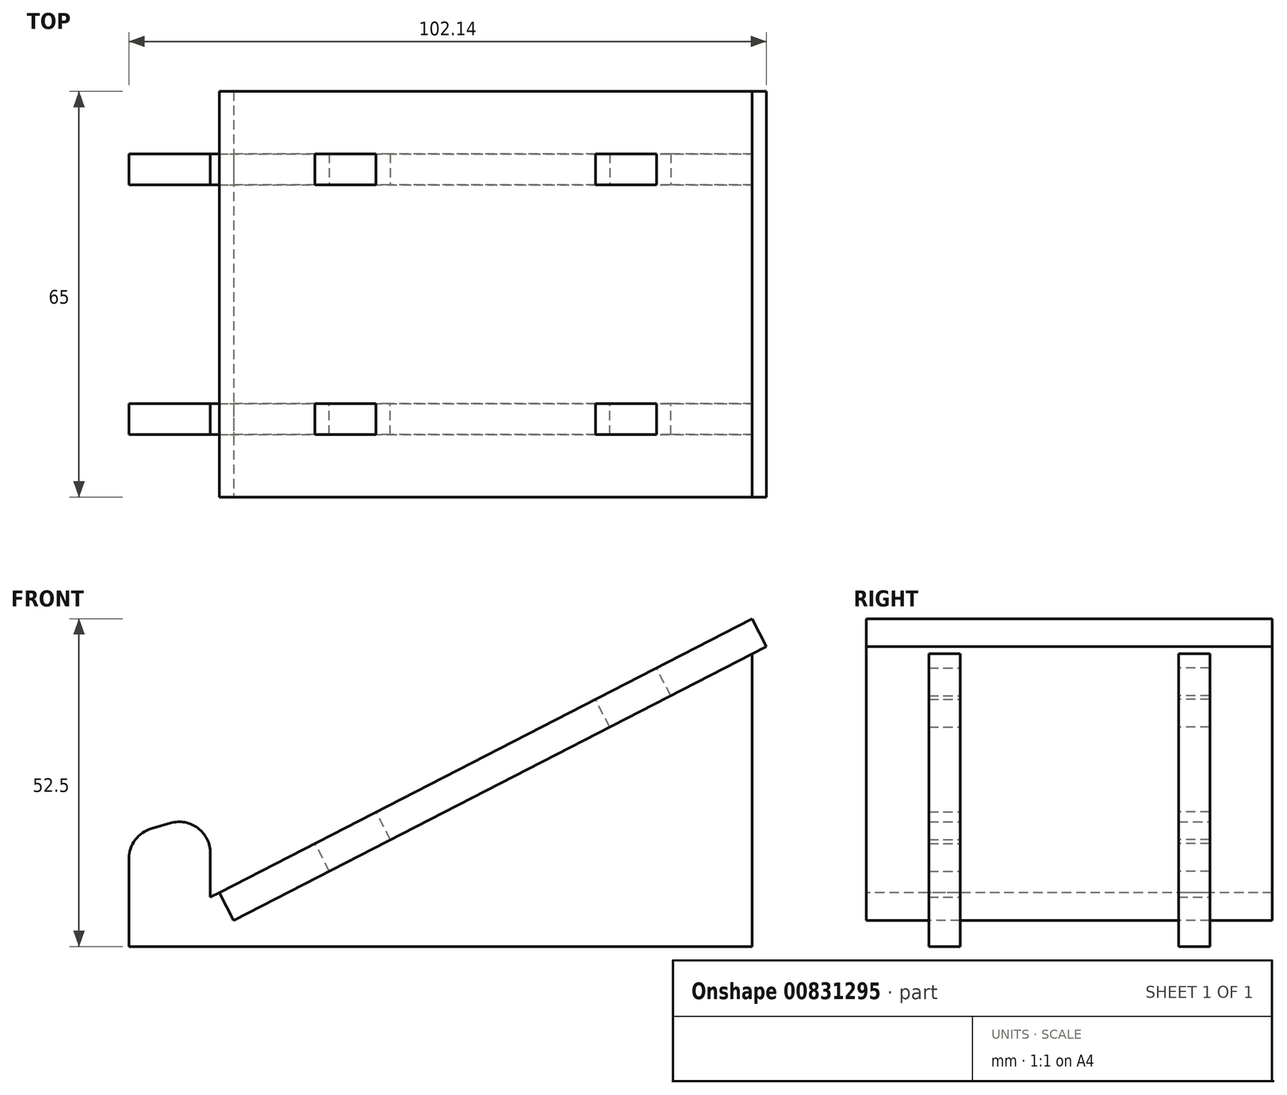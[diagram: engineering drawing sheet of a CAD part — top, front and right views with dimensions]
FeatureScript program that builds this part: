
annotation { "Feature Type Name" : "Feature", "Feature Type Description" : "" }
export const myFeature = defineFeature(function(context is Context, id is Id, definition is map)
    precondition{}
    {
        {
            var Q0;
            Q0=qCreatedBy(makeId("Front.planeOp"),FACE);
            var sketch = newSketch(context, id + "F0", { "sketchPlane" : qUnion([Q0])});
            skLineSegment(sketch, "E0", {"start": v(41.7, 0) * mm, "end": v(41.7, 52.5) * mm});
            skLineSegment(sketch, "E1", {"start": v(41.7, 52.5) * mm, "end": v(-45.12, 7.9) * mm});
            skLineSegment(sketch, "E2", {"start": v(-45.12, 7.9) * mm, "end": v(-45.12, 21.62) * mm});
            skLineSegment(sketch, "E3", {"start": v(-45.12, 21.62) * mm, "end": v(-58.16, 17.84) * mm});
            skLineSegment(sketch, "E4", {"start": v(-58.16, 17.84) * mm, "end": v(-58.16, 0) * mm});
            skLineSegment(sketch, "E5", {"start": v(-58.16, 0) * mm, "end": v(41.7, 0) * mm});
            skSolve(sketch);
        }
        {
            assignVariable(context, id + "F1", {"name" : "w", "anyValue" : 5});
        }
        {
            var Q0;
            Q0=makeQuery(id+"F0.imprint","IMPRINT",FACE,{"disambiguationData":[TD([[makeQuery(id+"F0.imprint","IMPRINT",EDGE,{"derivedFrom":sQuery(id+"F0.wireOp",EDGE,"E0")}),1.0]])]});
            extrude(context, id + "F2", {"entities" : qUnion([Q0]), "depth" : (getVariable(context, 'w')) * mm, "offsetDistance" : 25 * mm});
        }
        {
            var Q0;
            Q0=makeQuery(id+"F2.opExtrude","SWEPT_BODY",BODY,{"disambiguationData":[OSD([sQuery(id+"F0.wireOp",EDGE,"E0"),sQuery(id+"F0.wireOp",EDGE,"E1"),sQuery(id+"F0.wireOp",EDGE,"E2"),sQuery(id+"F0.wireOp",EDGE,"E3"),sQuery(id+"F0.wireOp",EDGE,"E4"),sQuery(id+"F0.wireOp",EDGE,"E5")])]});
            transform(context, id + "F3", {"entities" : qUnion([Q0]), "transformType" : TransformType.TRANSLATION_3D, "dx" : 0 * mm, "dy" : -40 * mm, "dz" : 0 * mm, "makeCopy" : true});
        }
        {
            var Q0;
            Q0=makeQuery(id+"F2.opExtrude","SWEPT_FACE",FACE,{"disambiguationData":[OSD([sQuery(id+"F0.wireOp",EDGE,"E1")])]});
            var sketch = newSketch(context, id + "F4", { "sketchPlane" : qUnion([Q0])});
            skLineSegment(sketch, "E6.bottom", {"start": v(61.08, 10) * mm, "end": v(-34.92, 10) * mm});
            skLineSegment(sketch, "E6.top", {"start": v(61.08, -55) * mm, "end": v(-34.92, -55) * mm});
            skLineSegment(sketch, "E6.left", {"start": v(61.08, 10) * mm, "end": v(61.08, -55) * mm});
            skLineSegment(sketch, "E6.right", {"start": v(-34.92, 10) * mm, "end": v(-34.92, -55) * mm});
            skLineSegment(sketch, "E7", {"start": v(13.08, 10) * mm, "end": v(13.08, -55) * mm, "construction": true});
            skLineSegment(sketch, "E8", {"start": v(61.08, -22.5) * mm, "end": v(-34.92, -22.5) * mm, "construction": true});
            skLineSegment(sketch, "E9.bottom", {"start": v(43.83, 0) * mm, "end": v(32.83, 0) * mm});
            skLineSegment(sketch, "E9.top", {"start": v(43.83, -5) * mm, "end": v(32.83, -5) * mm});
            skLineSegment(sketch, "E9.left", {"start": v(43.83, 0) * mm, "end": v(43.83, -5) * mm});
            skLineSegment(sketch, "E9.right", {"start": v(32.83, 0) * mm, "end": v(32.83, -5) * mm});
            skLineSegment(sketch, "E10.MirrorCS", {"start": v(-17.67, 0) * mm, "end": v(-6.67, 0) * mm});
            skLineSegment(sketch, "E11.MirrorCS", {"start": v(-17.67, -5) * mm, "end": v(-6.67, -5) * mm});
            skLineSegment(sketch, "E12.MirrorCS", {"start": v(-6.67, 0) * mm, "end": v(-6.67, -5) * mm});
            skLineSegment(sketch, "E13.MirrorCS", {"start": v(-17.67, 0) * mm, "end": v(-17.67, -5) * mm});
            skLineSegment(sketch, "E14.MirrorCS", {"start": v(-17.67, -45) * mm, "end": v(-17.67, -40) * mm});
            skLineSegment(sketch, "E15.MirrorCS", {"start": v(-6.67, -45) * mm, "end": v(-6.67, -40) * mm});
            skLineSegment(sketch, "E16.MirrorCS", {"start": v(-17.67, -40) * mm, "end": v(-6.67, -40) * mm});
            skLineSegment(sketch, "E17.MirrorCS", {"start": v(-17.67, -45) * mm, "end": v(-6.67, -45) * mm});
            skLineSegment(sketch, "E18.MirrorCS", {"start": v(43.83, -45) * mm, "end": v(32.83, -45) * mm});
            skLineSegment(sketch, "E19.MirrorCS", {"start": v(43.83, -45) * mm, "end": v(43.83, -40) * mm});
            skLineSegment(sketch, "E20.MirrorCS", {"start": v(32.83, -45) * mm, "end": v(32.83, -40) * mm});
            skLineSegment(sketch, "E21.MirrorCS", {"start": v(43.83, -40) * mm, "end": v(32.83, -40) * mm});
            skSolve(sketch);
        }
        {
            var Q0;
            {var subQ0=sQuery(id+"F4.wireOp",EDGE,"E9.right");Q0=makeQuery(id+"F4.imprint","IMPRINT",FACE,{"disambiguationData":[TD([[makeQuery(id+"F4.imprint","IMPRINT",EDGE,{"derivedFrom":subQ0}),-1.0]])]});}
            var Q1;
            {var subQ6=sQuery(id+"F4.wireOp",EDGE,"E9.left");Q1=makeQuery(id+"F4.imprint","IMPRINT",FACE,{"disambiguationData":[TD([[makeQuery(id+"F4.imprint","IMPRINT",EDGE,{"derivedFrom":subQ6}),1.0]])]});}
            var Q2;
            {var subQ4=sQuery(id+"F4.wireOp",EDGE,"E6.bottom");Q2=makeQuery(id+"F4.imprint","IMPRINT",FACE,{"disambiguationData":[TD([[makeQuery(id+"F4.imprint","IMPRINT",EDGE,{"derivedFrom":subQ4}),1.0]])]});}
            var Q3;
            {var subQ1=sQuery(id+"F4.wireOp",EDGE,"E6.top");Q3=makeQuery(id+"F4.imprint","IMPRINT",FACE,{"disambiguationData":[TD([[makeQuery(id+"F4.imprint","IMPRINT",EDGE,{"derivedFrom":subQ1}),-1.0]])]});}
            var Q4;
            {var subQ6=sQuery(id+"F4.wireOp",EDGE,"E13.MirrorCS");Q4=makeQuery(id+"F4.imprint","IMPRINT",FACE,{"disambiguationData":[TD([[makeQuery(id+"F4.imprint","IMPRINT",EDGE,{"derivedFrom":subQ6}),-1.0]])]});}
            extrude(context, id + "F5", {"entities" : qUnion([Q0, Q1, Q2, Q3, Q4]), "oppositeDirection" : true, "depth" : (getVariable(context, 'w')) * mm, "offsetDistance" : 25 * mm});
        }
        {
            var Q0;
            Q0=makeQuery(id+"F5.opExtrude","SWEPT_BODY",BODY,{"disambiguationData":[OSD([sQuery(id+"F4.wireOp",EDGE,"E6.bottom"),sQuery(id+"F4.wireOp",EDGE,"E6.top"),sQuery(id+"F4.wireOp",EDGE,"E6.left"),sQuery(id+"F4.wireOp",EDGE,"E6.right"),sQuery(id+"F4.wireOp",EDGE,"E9.bottom"),sQuery(id+"F4.wireOp",EDGE,"E9.top"),sQuery(id+"F4.wireOp",EDGE,"E9.left"),sQuery(id+"F4.wireOp",EDGE,"E9.right"),sQuery(id+"F4.wireOp",EDGE,"E10.MirrorCS"),sQuery(id+"F4.wireOp",EDGE,"E11.MirrorCS"),sQuery(id+"F4.wireOp",EDGE,"E12.MirrorCS"),sQuery(id+"F4.wireOp",EDGE,"E13.MirrorCS"),sQuery(id+"F4.wireOp",EDGE,"E14.MirrorCS"),sQuery(id+"F4.wireOp",EDGE,"E15.MirrorCS"),sQuery(id+"F4.wireOp",EDGE,"E16.MirrorCS"),sQuery(id+"F4.wireOp",EDGE,"E17.MirrorCS"),sQuery(id+"F4.wireOp",EDGE,"E18.MirrorCS"),sQuery(id+"F4.wireOp",EDGE,"E19.MirrorCS"),sQuery(id+"F4.wireOp",EDGE,"E20.MirrorCS"),sQuery(id+"F4.wireOp",EDGE,"E21.MirrorCS")])]});
            var Q1;
            Q1=makeQuery(id+"F3.opPattern","COPY",BODY,{"derivedFrom":makeQuery(id+"F2.opExtrude","SWEPT_BODY",BODY,{"disambiguationData":[OSD([sQuery(id+"F0.wireOp",EDGE,"E0"),sQuery(id+"F0.wireOp",EDGE,"E1"),sQuery(id+"F0.wireOp",EDGE,"E2"),sQuery(id+"F0.wireOp",EDGE,"E3"),sQuery(id+"F0.wireOp",EDGE,"E4"),sQuery(id+"F0.wireOp",EDGE,"E5")])]}),"instanceName":"1"});
            var Q2;
            Q2=makeQuery(id+"F2.opExtrude","SWEPT_BODY",BODY,{"disambiguationData":[OSD([sQuery(id+"F0.wireOp",EDGE,"E0"),sQuery(id+"F0.wireOp",EDGE,"E1"),sQuery(id+"F0.wireOp",EDGE,"E2"),sQuery(id+"F0.wireOp",EDGE,"E3"),sQuery(id+"F0.wireOp",EDGE,"E4"),sQuery(id+"F0.wireOp",EDGE,"E5")])]});
            booleanBodies(context, id + "F6", {"operationType" : BooleanOperationType.SUBTRACTION, "tools" : qUnion([Q0]), "targets" : qUnion([Q1, Q2]), "keepTools" : true});
        }
        {
            var Q0;
            Q0=makeQuery(id+"F2.opExtrude","SWEPT_EDGE",EDGE,{"disambiguationData":[OSD([sQuery(id+"F0.wireOp",EDGE,"E2"),sQuery(id+"F0.wireOp",EDGE,"E3")])]});
            var Q1;
            Q1=makeQuery(id+"F3.opPattern","COPY",EDGE,{"derivedFrom":makeQuery(id+"F2.opExtrude","SWEPT_EDGE",EDGE,{"disambiguationData":[OSD([sQuery(id+"F0.wireOp",EDGE,"E2"),sQuery(id+"F0.wireOp",EDGE,"E3")])]}),"instanceName":"1"});
            var Q2;
            Q2=makeQuery(id+"F3.opPattern","COPY",EDGE,{"derivedFrom":makeQuery(id+"F2.opExtrude","SWEPT_EDGE",EDGE,{"disambiguationData":[OSD([sQuery(id+"F0.wireOp",EDGE,"E3"),sQuery(id+"F0.wireOp",EDGE,"E4")])]}),"instanceName":"1"});
            var Q3;
            Q3=makeQuery(id+"F2.opExtrude","SWEPT_EDGE",EDGE,{"disambiguationData":[OSD([sQuery(id+"F0.wireOp",EDGE,"E3"),sQuery(id+"F0.wireOp",EDGE,"E4")])]});
            fillet(context, id + "F7", {"entities" : qUnion([Q0, Q1, Q2, Q3]), "radius" : 5 * mm, "tangentPropagation" : true, "allowEdgeOverflow" : false});
        }
    });
